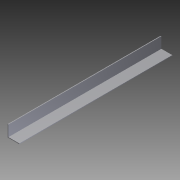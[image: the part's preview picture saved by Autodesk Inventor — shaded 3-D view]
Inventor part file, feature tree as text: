
AUTODESK INVENTOR PART (.ipt)
format: ipt  version: 2012 (Build 160160000, 160)  size: 71,680 bytes
history: native  units: in
note: dims shown in document units (in); Inventor stores cm internally (conversion verified against a paired STEP export)
features: extrude x1, sketch x1
ambient origin geometry x8: Origin, YZ Plane, XZ Plane, XY Plane, X Axis, Y Axis, Z Axis, Center Point
bodies: Solid1 (feature_tree)
feature tree (2):
  extrude  "Extrusion1"  Depth=0.0625in
  sketch  "Sketch1"  dims[d0=0.0625in d1=0.0625in d2=1.0in d3=1.0in d4=13.125in d5=0.0in]
